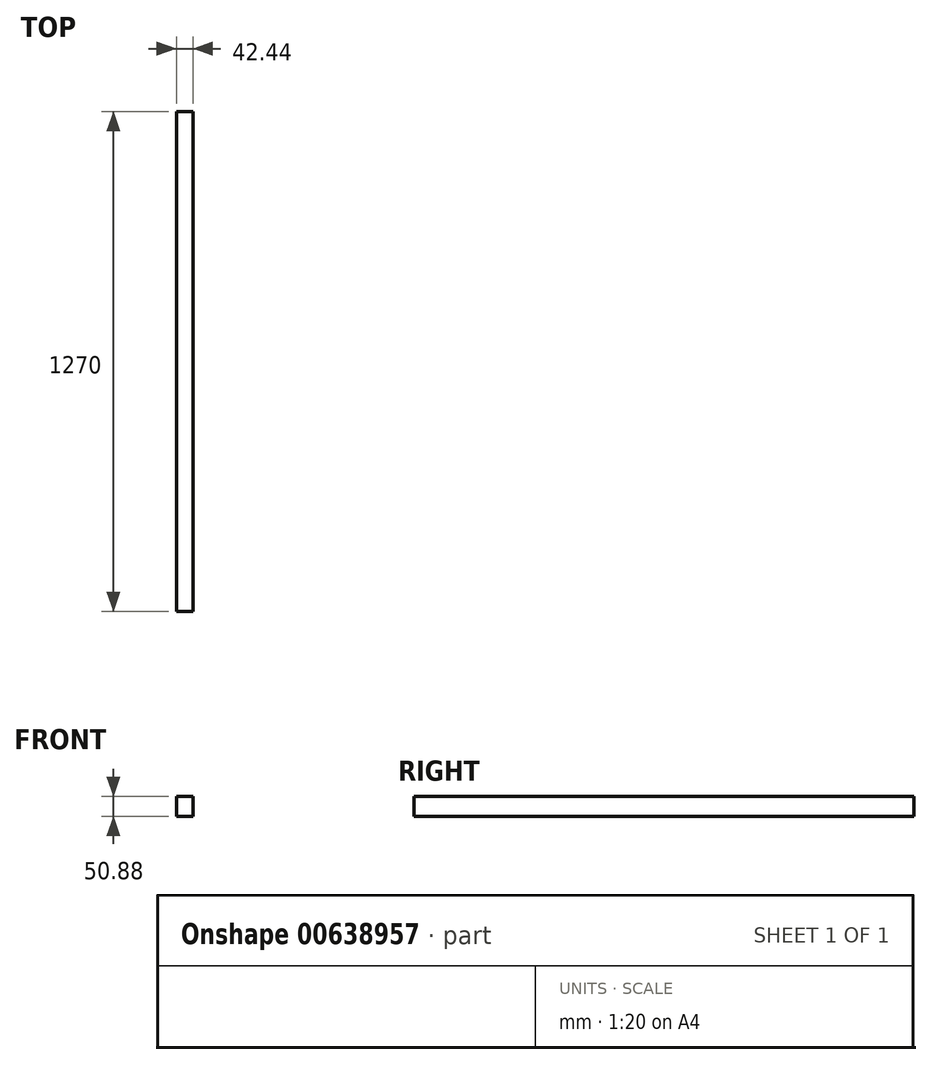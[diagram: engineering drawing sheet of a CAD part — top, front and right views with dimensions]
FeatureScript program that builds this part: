
annotation { "Feature Type Name" : "Feature", "Feature Type Description" : "" }
export const myFeature = defineFeature(function(context is Context, id is Id, definition is map)
    precondition{}
    {
        {
            var Q0;
            Q0=qCreatedBy(makeId("Front.planeOp"),FACE);
            var sketch = newSketch(context, id + "F0", { "sketchPlane" : qUnion([Q0])});
            skLineSegment(sketch, "E0.bottom", {"start": v(-42.44, 50.88) * mm, "end": v(0, 50.88) * mm});
            skLineSegment(sketch, "E0.top", {"start": v(-42.44, 0) * mm, "end": v(0, 0) * mm});
            skLineSegment(sketch, "E0.left", {"start": v(-42.44, 50.88) * mm, "end": v(-42.44, 0) * mm});
            skLineSegment(sketch, "E0.right", {"start": v(0, 50.88) * mm, "end": v(0, 0) * mm});
            skSolve(sketch);
        }
        {
            var Q0;
            Q0 = qSketchRegion(id + "F0", true);
            extrude(context, id + "F1", {"entities" : qUnion([Q0]), "depth" : 1270 * mm, "offsetDistance" : 25.4 * mm});
        }
    });
